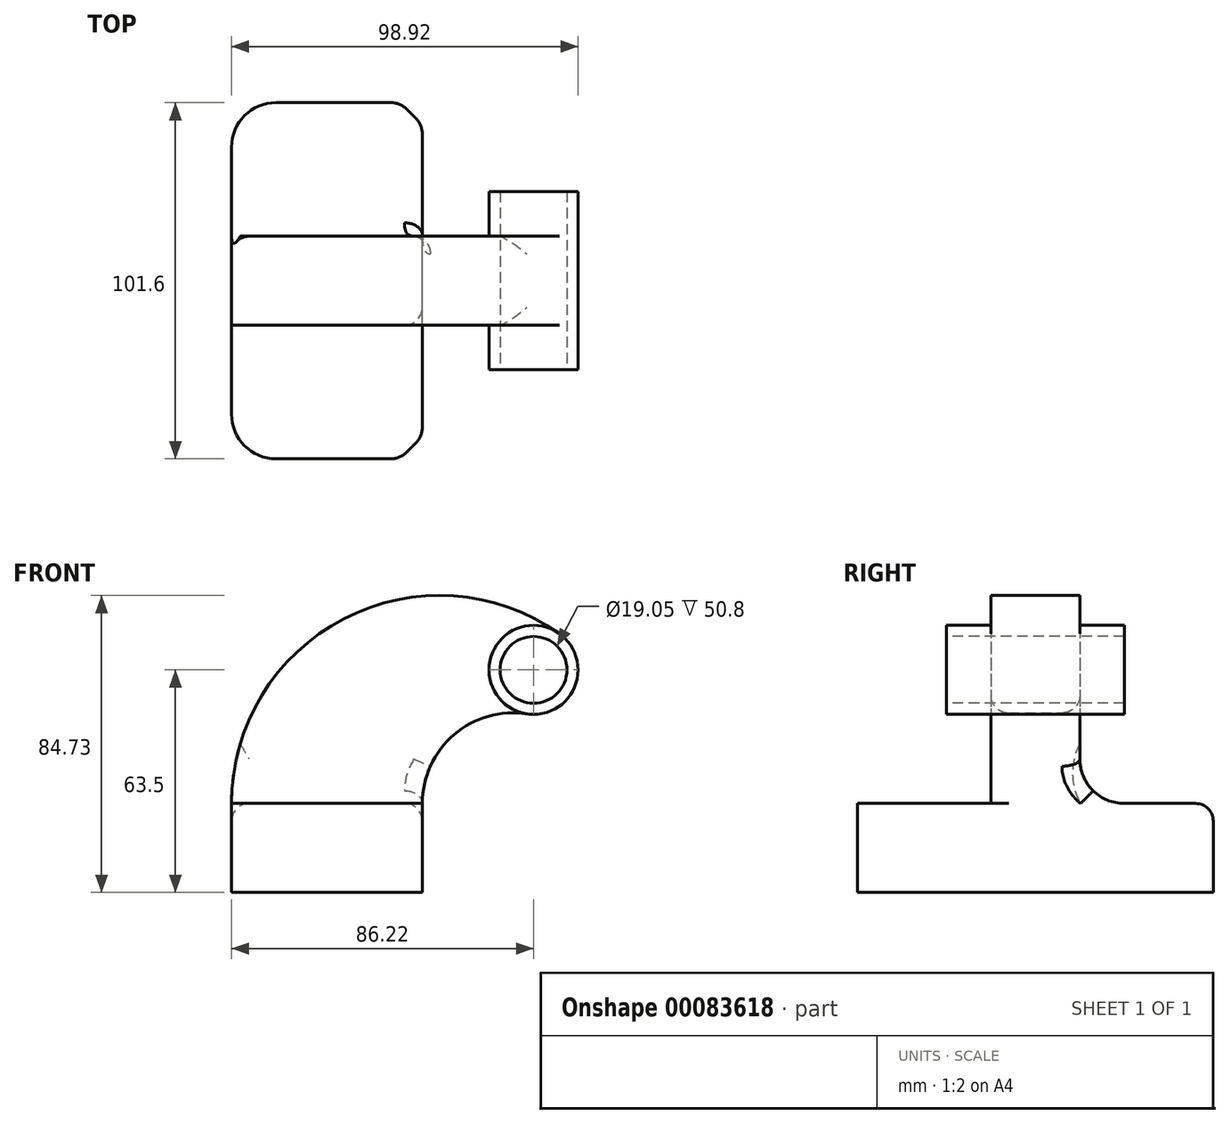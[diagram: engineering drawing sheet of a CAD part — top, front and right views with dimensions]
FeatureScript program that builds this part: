
annotation { "Feature Type Name" : "Feature", "Feature Type Description" : "" }
export const myFeature = defineFeature(function(context is Context, id is Id, definition is map)
    precondition{}
    {
        {
            var Q0;
            Q0=qCreatedBy(makeId("Front.planeOp"),FACE);
            var sketch = newSketch(context, id + "F0", { "sketchPlane" : qUnion([Q0])});
            skLineSegment(sketch, "E0.bottom", {"start": v(-54.47, 0) * mm, "end": v(0, 0) * mm});
            skLineSegment(sketch, "E0.top", {"start": v(-54.47, -25.4) * mm, "end": v(0, -25.4) * mm});
            skLineSegment(sketch, "E0.left", {"start": v(-54.47, 0) * mm, "end": v(-54.47, -25.4) * mm});
            skLineSegment(sketch, "E0.right", {"start": v(0, 0) * mm, "end": v(0, -25.4) * mm});
            skCircle(sketch, "E1", {"center": v(31.75, 38.1) * mm, "radius": 12.7 * mm});
            skArc(sketch, "E2", {"start": v(0, 0) * mm, "mid": v(9.03, 19.63) * mm, "end": v(29.8, 25.55) * mm});
            skArc(sketch, "E3", {"start": v(-54.47, 0) * mm, "mid": v(-22.44, 52.68) * mm, "end": v(39.07, 48.48) * mm});
            skSolve(sketch);
        }
        {
            var Q0;
            Q0=makeQuery(id+"F0.imprint","IMPRINT",FACE,{"disambiguationData":[TD([[makeQuery(id+"F0.imprint","IMPRINT",EDGE,{"derivedFrom":sQuery(id+"F0.wireOp",EDGE,"E0.bottom")}),-1.0]])]});
            extrude(context, id + "F1", {"entities" : qUnion([Q0]), "endBound" : BoundingType.SYMMETRIC, "depth" : 101.6 * mm});
        }
        {
            var Q0;
            Q0=makeQuery(id+"F0.imprint","IMPRINT",FACE,{"disambiguationData":[TD([[makeQuery(id+"F0.imprint","IMPRINT",EDGE,{"derivedFrom":sQuery(id+"F0.wireOp",EDGE,"E0.bottom")}),1.0]])]});
            extrude(context, id + "F2", {"entities" : qUnion([Q0]), "operationType" : NewBodyOperationType.ADD, "endBound" : BoundingType.SYMMETRIC, "depth" : 25.4 * mm});
        }
        {
            var Q0;
            {var subQ0=sQuery(id+"F0.wireOp",EDGE,"E1");var subQ1=makeQuery(id+"F0.imprint","INTERSECT",VERTEX,{"derivedFrom":[subQ0,sQuery(id+"F0.wireOp",EDGE,"E2")]});Q0=makeQuery(id+"F0.imprint","IMPRINT",FACE,{"disambiguationData":[TD([[makeQuery(id+"F0.imprint","IMPRINT",EDGE,{"disambiguationData":[TD([[subQ1,1.0]])],"derivedFrom":subQ0}),1.0]])]});}
            extrude(context, id + "F3", {"entities" : qUnion([Q0]), "operationType" : NewBodyOperationType.ADD, "endBound" : BoundingType.SYMMETRIC, "depth" : 50.8 * mm});
        }
        {
            var Q0;
            Q0=makeQuery(id+"F3.opExtrude","CAP_FACE",FACE,{"disambiguationData":[OSD([sQuery(id+"F0.wireOp",EDGE,"E1")])],"isStart":false});
            var sketch = newSketch(context, id + "F4", { "sketchPlane" : qUnion([Q0])});
            skPoint(sketch, "E4", {"position": v(31.75, 38.1) * mm});
            skSolve(sketch);
        }
        {
            var Q0;
            Q0=sQuery(id+"F4.wireOp",VERTEX,"E4");
            var Q1;
            Q1=makeQuery(id+"F1.opExtrude","SWEPT_BODY",BODY,{"disambiguationData":[OSD([sQuery(id+"F0.wireOp",EDGE,"E0.bottom"),sQuery(id+"F0.wireOp",EDGE,"E0.top"),sQuery(id+"F0.wireOp",EDGE,"E0.left"),sQuery(id+"F0.wireOp",EDGE,"E0.right")])]});
            hole(context, id + "F5", {"style" : HoleStyle.SIMPLE, "endStyle" : HoleEndStyle.THROUGH, "holeDiameter" : 19.05 * mm, "locations" : qUnion([Q0]), "scope" : qUnion([Q1]), "isTappedThrough" : true});
        }
        {
            var Q0;
            Q0=makeQuery(id+"F1.opExtrude","CAP_EDGE",EDGE,{"disambiguationData":[OSD([sQuery(id+"F0.wireOp",EDGE,"E0.right")])],"isStart":false});
            var Q1;
            Q1=makeQuery(id+"F1.opExtrude","CAP_EDGE",EDGE,{"disambiguationData":[OSD([sQuery(id+"F0.wireOp",EDGE,"E0.right")])],"isStart":true});
            chamfer(context, id + "F6", {"entities" : qUnion([Q0, Q1]), "width" : 6.35 * mm, "tangentPropagation" : true});
        }
        {
            var Q0;
            Q0=makeQuery(id+"F1.opExtrude","CAP_EDGE",EDGE,{"disambiguationData":[OSD([sQuery(id+"F0.wireOp",EDGE,"E0.left")])],"isStart":false});
            var Q1;
            Q1=makeQuery(id+"F1.opExtrude","CAP_EDGE",EDGE,{"disambiguationData":[OSD([sQuery(id+"F0.wireOp",EDGE,"E0.left")])],"isStart":true});
            fillet(context, id + "F7", {"entities" : qUnion([Q0, Q1]), "radius" : 12.7 * mm, "tangentPropagation" : true, "allowEdgeOverflow" : false});
        }
        {
            var Q0;
            {var subQ0=sQuery(id+"F0.wireOp",EDGE,"E0.right");Q0=makeQuery(id+"F6.opChamfer","BLEND_EDGE",EDGE,{"blendedFrom":[makeQuery(id+"F1.opExtrude","CAP_EDGE",EDGE,{"disambiguationData":[OSD([subQ0])],"isStart":false}),makeQuery(id+"F1.opExtrude","CAP_FACE",FACE,{"disambiguationData":[OSD([sQuery(id+"F0.wireOp",EDGE,"E0.bottom"),sQuery(id+"F0.wireOp",EDGE,"E0.top"),sQuery(id+"F0.wireOp",EDGE,"E0.left"),subQ0])],"isStart":false})],"blendedInto":[makeQuery(id+"F1.opExtrude","CAP_FACE",FACE,{"disambiguationData":[OSD([sQuery(id+"F0.wireOp",EDGE,"E0.bottom"),sQuery(id+"F0.wireOp",EDGE,"E0.top"),sQuery(id+"F0.wireOp",EDGE,"E0.left"),subQ0])],"isStart":false})]});}
            var Q1;
            {var subQ0=sQuery(id+"F0.wireOp",EDGE,"E0.right");Q1=makeQuery(id+"F6.opChamfer","BLEND_EDGE",EDGE,{"blendedFrom":[makeQuery(id+"F1.opExtrude","CAP_EDGE",EDGE,{"disambiguationData":[OSD([subQ0])],"isStart":false}),makeQuery(id+"F1.opExtrude","SWEPT_FACE",FACE,{"disambiguationData":[OSD([subQ0])]})],"blendedInto":[makeQuery(id+"F1.opExtrude","SWEPT_FACE",FACE,{"disambiguationData":[OSD([subQ0])]})]});}
            var Q2;
            {var subQ0=sQuery(id+"F0.wireOp",EDGE,"E0.right");Q2=makeQuery(id+"F6.opChamfer","BLEND_EDGE",EDGE,{"blendedFrom":[makeQuery(id+"F1.opExtrude","CAP_EDGE",EDGE,{"disambiguationData":[OSD([subQ0])],"isStart":true}),makeQuery(id+"F1.opExtrude","CAP_FACE",FACE,{"disambiguationData":[OSD([sQuery(id+"F0.wireOp",EDGE,"E0.bottom"),sQuery(id+"F0.wireOp",EDGE,"E0.top"),sQuery(id+"F0.wireOp",EDGE,"E0.left"),subQ0])],"isStart":true})],"blendedInto":[makeQuery(id+"F1.opExtrude","CAP_FACE",FACE,{"disambiguationData":[OSD([sQuery(id+"F0.wireOp",EDGE,"E0.bottom"),sQuery(id+"F0.wireOp",EDGE,"E0.top"),sQuery(id+"F0.wireOp",EDGE,"E0.left"),subQ0])],"isStart":true})]});}
            var Q3;
            {var subQ0=sQuery(id+"F0.wireOp",EDGE,"E0.right");Q3=makeQuery(id+"F6.opChamfer","BLEND_EDGE",EDGE,{"blendedFrom":[makeQuery(id+"F1.opExtrude","CAP_EDGE",EDGE,{"disambiguationData":[OSD([subQ0])],"isStart":true}),makeQuery(id+"F1.opExtrude","SWEPT_FACE",FACE,{"disambiguationData":[OSD([subQ0])]})],"blendedInto":[makeQuery(id+"F1.opExtrude","SWEPT_FACE",FACE,{"disambiguationData":[OSD([subQ0])]})]});}
            fillet(context, id + "F8", {"entities" : qUnion([Q0, Q1, Q2, Q3]), "radius" : 6.35 * mm, "tangentPropagation" : true, "allowEdgeOverflow" : false});
        }
        {
            var Q0;
            Q0=makeQuery(id+"F2.opExtrude","CAP_EDGE",EDGE,{"disambiguationData":[OSD([sQuery(id+"F0.wireOp",EDGE,"E0.bottom")])],"isStart":true});
            var Q1;
            Q1=makeQuery(id+"F2.opExtrude","CAP_EDGE",EDGE,{"disambiguationData":[OSD([sQuery(id+"F0.wireOp",EDGE,"E0.bottom")])],"isStart":false});
            fillet(context, id + "F9", {"entities" : qUnion([Q0, Q1]), "radius" : 12.7 * mm, "tangentPropagation" : true, "allowEdgeOverflow" : false});
        }
        {
            var Q0;
            Q0=makeQuery(id+"F2.opExtrude","CAP_EDGE",EDGE,{"disambiguationData":[OSD([sQuery(id+"F0.wireOp",EDGE,"E2")])],"isStart":false});
            var Q1;
            Q1=makeQuery(id+"F9.opFillet","BLEND_EDGE",EDGE,{"blendedFrom":[makeQuery(id+"F2.opExtrude","CAP_EDGE",EDGE,{"disambiguationData":[OSD([sQuery(id+"F0.wireOp",EDGE,"E0.bottom")])],"isStart":true}),makeQuery(id+"F2.opExtrude","SWEPT_FACE",FACE,{"disambiguationData":[OSD([sQuery(id+"F0.wireOp",EDGE,"E2")])]})],"blendedInto":[makeQuery(id+"F2.opExtrude","SWEPT_FACE",FACE,{"disambiguationData":[OSD([sQuery(id+"F0.wireOp",EDGE,"E2")])]})]});
            fillet(context, id + "F10", {"entities" : qUnion([Q0, Q1]), "radius" : 5.08 * mm, "tangentPropagation" : true, "allowEdgeOverflow" : false});
        }
    });
